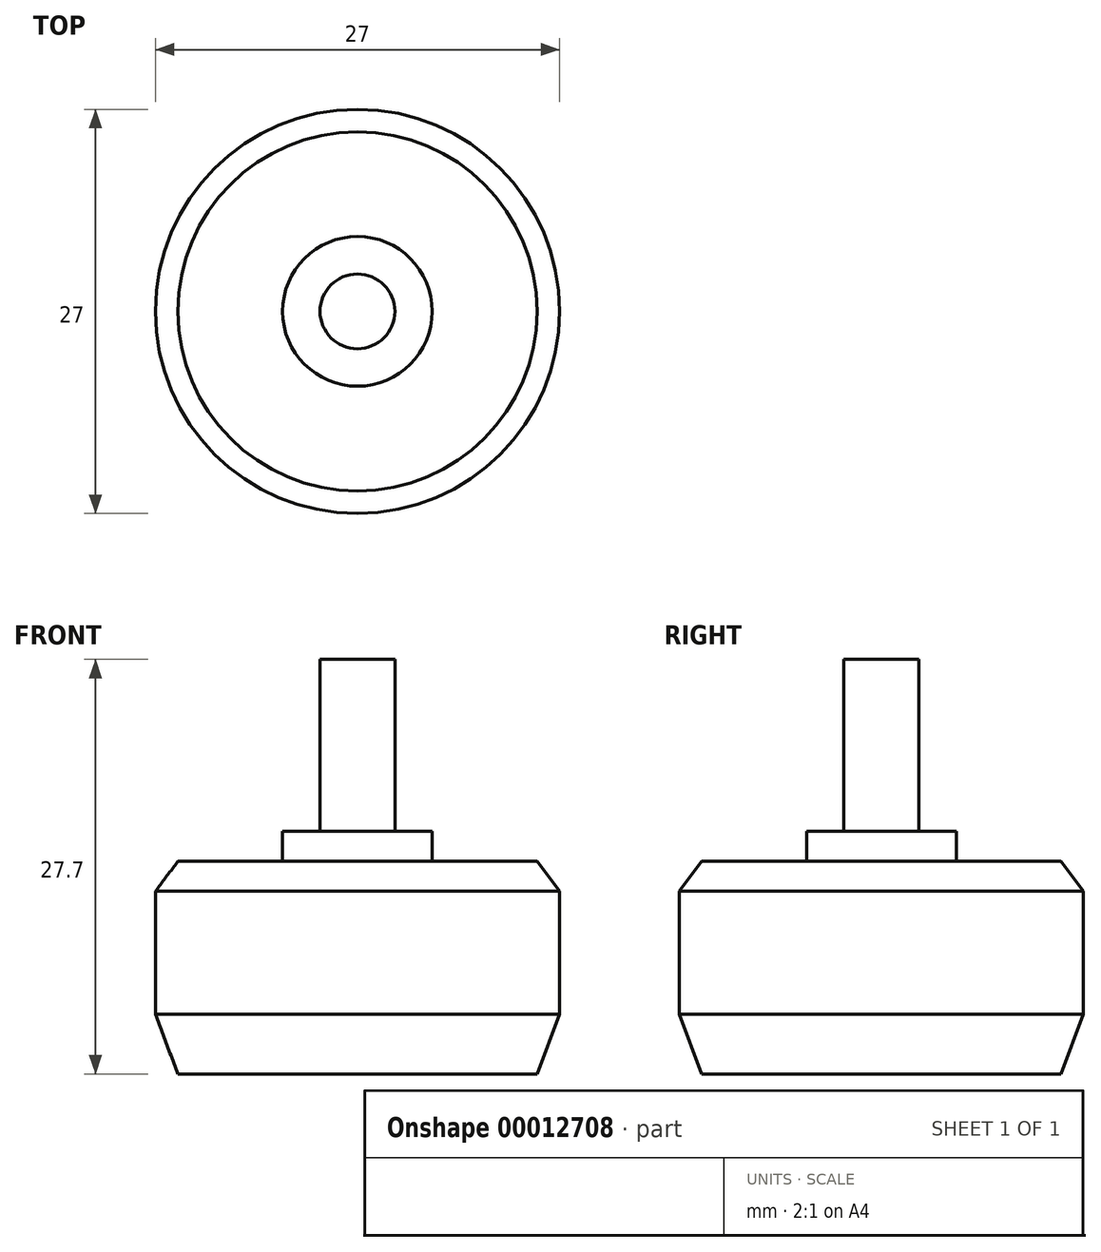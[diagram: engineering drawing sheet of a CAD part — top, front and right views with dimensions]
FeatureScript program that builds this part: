
annotation { "Feature Type Name" : "Feature", "Feature Type Description" : "" }
export const myFeature = defineFeature(function(context is Context, id is Id, definition is map)
    precondition{}
    {
        {
            var Q0;
            Q0=qCreatedBy(makeId("Front.planeOp"),FACE);
            var sketch = newSketch(context, id + "F0", { "sketchPlane" : qUnion([Q0])});
            skLineSegment(sketch, "E0", {"start": v(0, -16.4) * mm, "end": v(0, 34.86) * mm, "construction": true});
            skLineSegment(sketch, "E1", {"start": v(0, 0) * mm, "end": v(12, 0) * mm});
            skLineSegment(sketch, "E2", {"start": v(12, 0) * mm, "end": v(13.5, 4) * mm});
            skLineSegment(sketch, "E3", {"start": v(13.5, 4) * mm, "end": v(13.5, 12.2) * mm});
            skLineSegment(sketch, "E4", {"start": v(13.5, 12.2) * mm, "end": v(12, 14.2) * mm});
            skLineSegment(sketch, "E5", {"start": v(12, 14.2) * mm, "end": v(5, 14.2) * mm});
            skLineSegment(sketch, "E6", {"start": v(5, 14.2) * mm, "end": v(5, 16.2) * mm});
            skLineSegment(sketch, "E7", {"start": v(5, 16.2) * mm, "end": v(2.5, 16.2) * mm});
            skLineSegment(sketch, "E8", {"start": v(2.5, 16.2) * mm, "end": v(2.5, 27.7) * mm});
            skLineSegment(sketch, "E9", {"start": v(2.5, 27.7) * mm, "end": v(0, 27.7) * mm});
            skLineSegment(sketch, "E10", {"start": v(0, 27.7) * mm, "end": v(0, 0) * mm});
            skSolve(sketch);
        }
        {
            var Q0;
            Q0=makeQuery(id+"F0.imprint","IMPRINT",FACE,{"disambiguationData":[TD([[makeQuery(id+"F0.imprint","IMPRINT",EDGE,{"derivedFrom":sQuery(id+"F0.wireOp",EDGE,"E1")}),1.0]])]});
            var Q1;
            Q1=sQuery(id+"F0.wireOp",EDGE,"E0");
            revolve(context, id + "F1", {"entities" : qUnion([Q0]), "axis" : qUnion([Q1]), "revolveType" : RevolveType.FULL});
        }
    });
